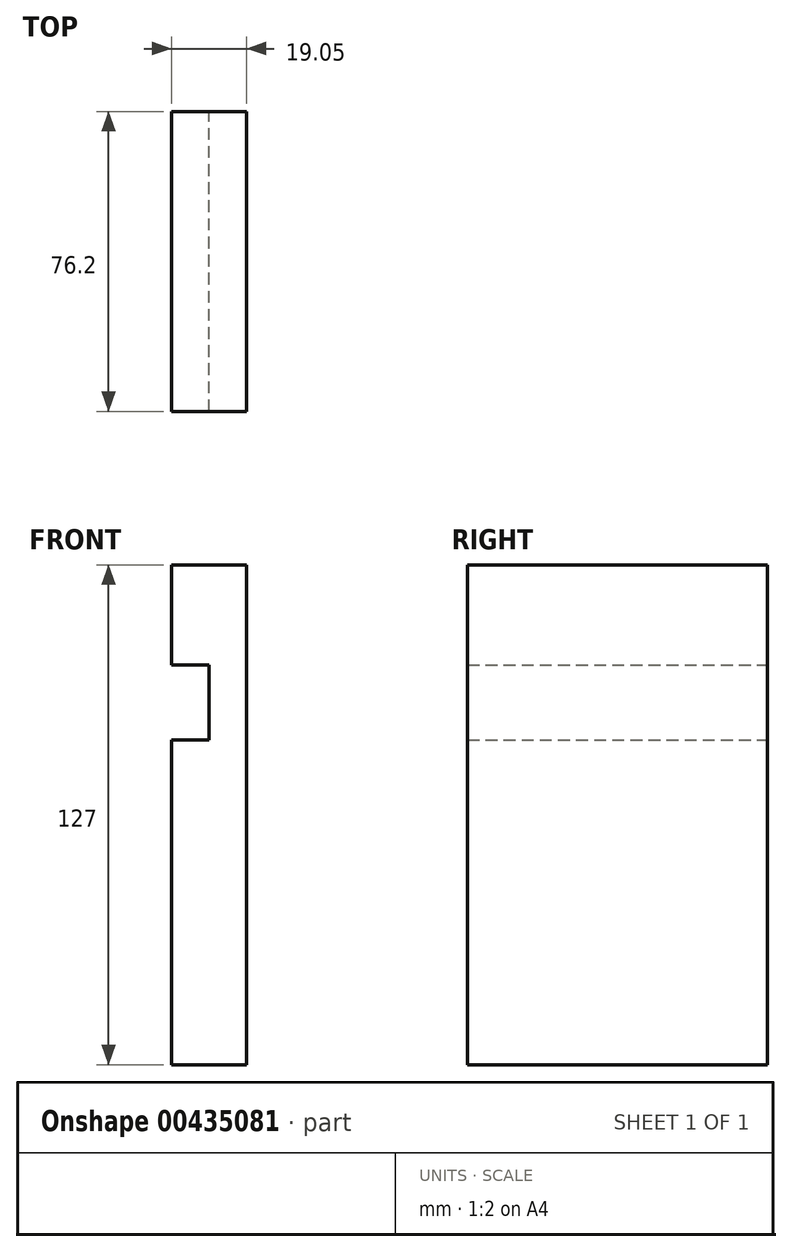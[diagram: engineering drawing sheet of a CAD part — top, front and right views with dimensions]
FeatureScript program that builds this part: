
annotation { "Feature Type Name" : "Feature", "Feature Type Description" : "" }
export const myFeature = defineFeature(function(context is Context, id is Id, definition is map)
    precondition{}
    {
        {
            var Q0;
            Q0=qCreatedBy(makeId("Front.planeOp"),FACE);
            var sketch = newSketch(context, id + "F0", { "sketchPlane" : qUnion([Q0])});
            skLineSegment(sketch, "E0", {"start": v(27, -72.5) * mm, "end": v(27, 54.5) * mm});
            skLineSegment(sketch, "E1", {"start": v(27, 54.5) * mm, "end": v(7.96, 54.5) * mm});
            skLineSegment(sketch, "E2", {"start": v(7.96, 54.5) * mm, "end": v(7.96, 29.1) * mm});
            skLineSegment(sketch, "E3", {"start": v(7.96, 29.1) * mm, "end": v(17.48, 29.1) * mm});
            skLineSegment(sketch, "E4", {"start": v(17.48, 29.1) * mm, "end": v(17.48, 10.04) * mm});
            skLineSegment(sketch, "E5", {"start": v(17.48, 10.04) * mm, "end": v(7.96, 10.04) * mm});
            skLineSegment(sketch, "E6", {"start": v(7.96, 10.04) * mm, "end": v(7.96, -72.06) * mm});
            skLineSegment(sketch, "E7", {"start": v(27, -72.5) * mm, "end": v(7.96, -72.5) * mm});
            skLineSegment(sketch, "E8", {"start": v(7.96, -72.5) * mm, "end": v(7.96, -67.5) * mm});
            skSolve(sketch);
        }
        {
            var Q0;
            Q0=qSketchRegion(id+"F0",true);
            extrude(context, id + "F1", {"entities" : qUnion([Q0]), "depth" : 76.2 * mm});
        }
    });
